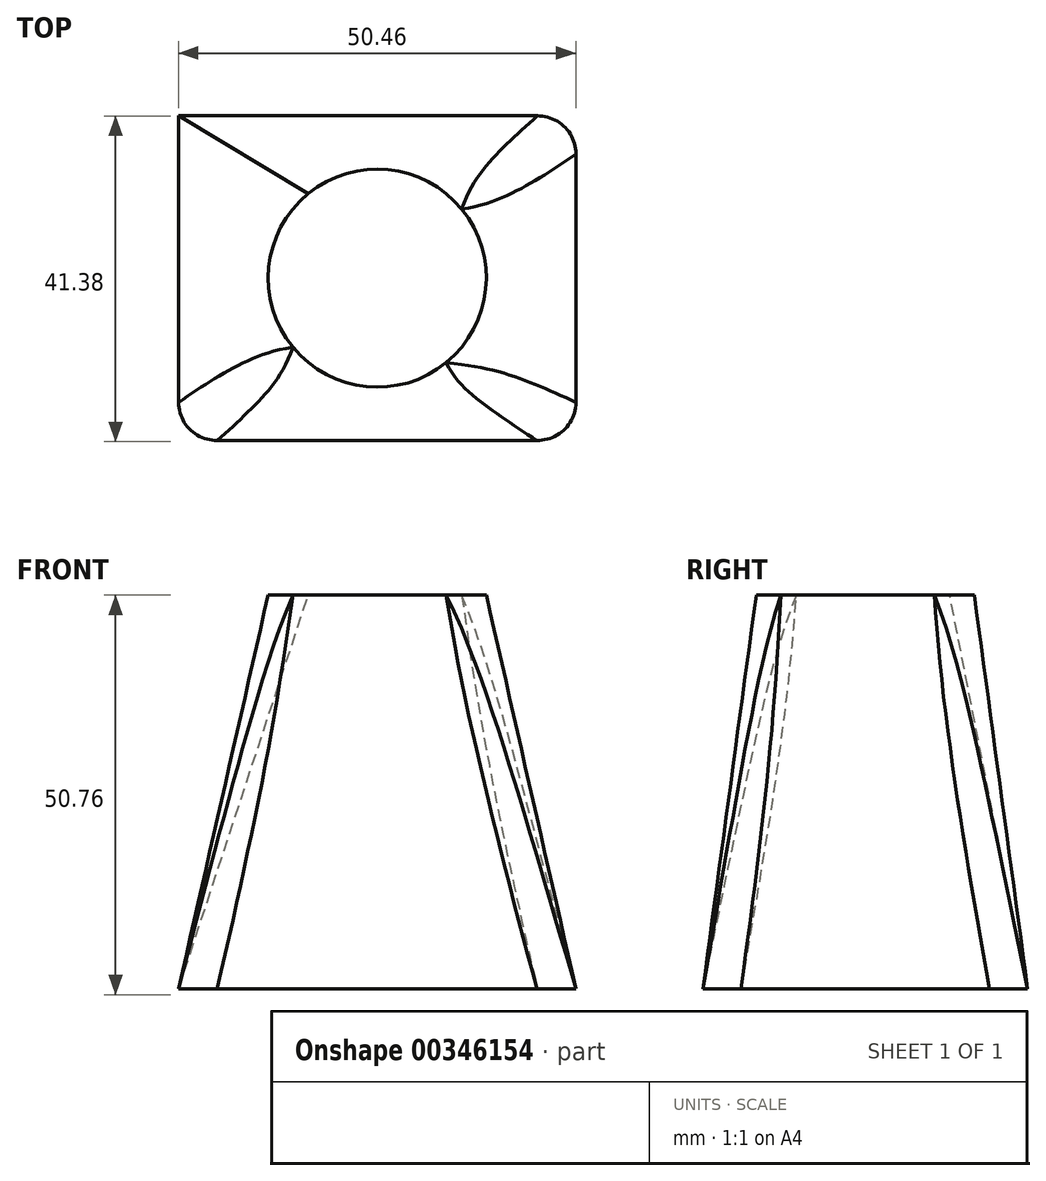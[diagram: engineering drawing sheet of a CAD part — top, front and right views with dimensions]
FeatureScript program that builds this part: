
annotation { "Feature Type Name" : "Feature", "Feature Type Description" : "" }
export const myFeature = defineFeature(function(context is Context, id is Id, definition is map)
    precondition{}
    {
        {
            var Q0;
            Q0=qCreatedBy(makeId("Top.planeOp"),FACE);
            var sketch = newSketch(context, id + "F0", { "sketchPlane" : qUnion([Q0])});
            skLineSegment(sketch, "E0.bottom", {"start": v(25.23, 20.62) * mm, "end": v(-25.23, 20.62) * mm});
            skLineSegment(sketch, "E0.top", {"start": v(25.23, -20.62) * mm, "end": v(-25.23, -20.62) * mm});
            skLineSegment(sketch, "E0.left", {"start": v(25.23, 20.62) * mm, "end": v(25.23, -20.62) * mm});
            skLineSegment(sketch, "E0.right", {"start": v(-25.23, 20.62) * mm, "end": v(-25.23, -20.62) * mm});
            skPoint(sketch, "E0.middle", {"position": v(0, 0) * mm});
            skSolve(sketch);
        }
        {
            var Q0;
            Q0=makeQuery(id+"F0.imprint","IMPRINT",FACE,{"disambiguationData":[TD([[makeQuery(id+"F0.imprint","IMPRINT",EDGE,{"derivedFrom":sQuery(id+"F0.wireOp",EDGE,"E0.bottom")}),1.0]])]});
            cPlane(context, id + "F1", {"entities" : qUnion([Q0]), "cplaneType" : CPlaneType.OFFSET, "offset" : 50 * mm, "width" : 150 * mm, "height" : 150 * mm});
        }
        {
            var Q0;
            Q0=qCreatedBy(id+"F1.planeOp",FACE);
            var sketch = newSketch(context, id + "F2", { "sketchPlane" : qUnion([Q0])});
            skCircle(sketch, "E1", {"center": v(0, 0) * mm, "radius": 13.85 * mm});
            skSolve(sketch);
        }
        {
            var Q0;
            Q0=makeQuery(id+"F0.imprint","IMPRINT",FACE,{"disambiguationData":[TD([[makeQuery(id+"F0.imprint","IMPRINT",EDGE,{"derivedFrom":sQuery(id+"F0.wireOp",EDGE,"E0.bottom")}),1.0]])]});
            var Q1;
            Q1=makeQuery(id+"F2.imprint","IMPRINT",FACE,{"disambiguationData":[TD([[makeQuery(id+"F2.imprint","IMPRINT",EDGE,{"derivedFrom":sQuery(id+"F2.wireOp",EDGE,"E1")}),1.0]])]});
            loft(context, id + "F3", {"sheetProfilesArray" : [{ "sheetProfileEntities" : qUnion([Q0]) }, { "sheetProfileEntities" : qUnion([Q1]) }]});
        }
        {
            var Q0;
            Q0=makeQuery(id+"F3.opLoft","SWEPT_EDGE",EDGE,{"disambiguationData":[OSD([sQuery(id+"F0.wireOp",EDGE,"E0.bottom"),sQuery(id+"F0.wireOp",EDGE,"E0.top"),sQuery(id+"F0.wireOp",EDGE,"E0.right"),sQuery(id+"F2.wireOp",EDGE,"E1")])]});
            var Q1;
            Q1=makeQuery(id+"F3.opLoft","SWEPT_EDGE",EDGE,{"disambiguationData":[OSD([sQuery(id+"F0.wireOp",EDGE,"E0.top"),sQuery(id+"F0.wireOp",EDGE,"E0.left"),sQuery(id+"F0.wireOp",EDGE,"E0.right"),sQuery(id+"F2.wireOp",EDGE,"E1")])]});
            var Q2;
            Q2=makeQuery(id+"F3.opLoft","SWEPT_EDGE",EDGE,{"disambiguationData":[OSD([sQuery(id+"F0.wireOp",EDGE,"E0.bottom"),sQuery(id+"F0.wireOp",EDGE,"E0.left")])]});
            var Q3;
            Q3=makeQuery(id+"F3.opLoft","SWEPT_EDGE",EDGE,{"disambiguationData":[OSD([sQuery(id+"F0.wireOp",EDGE,"E0.bottom"),sQuery(id+"F0.wireOp",EDGE,"E0.left"),sQuery(id+"F0.wireOp",EDGE,"E0.right"),sQuery(id+"F2.wireOp",EDGE,"E1")])]});
            fillet(context, id + "F4", {"entities" : qUnion([Q0, Q1, Q2, Q3]), "radius" : 5 * mm, "tangentPropagation" : true, "allowEdgeOverflow" : false});
        }
    });
